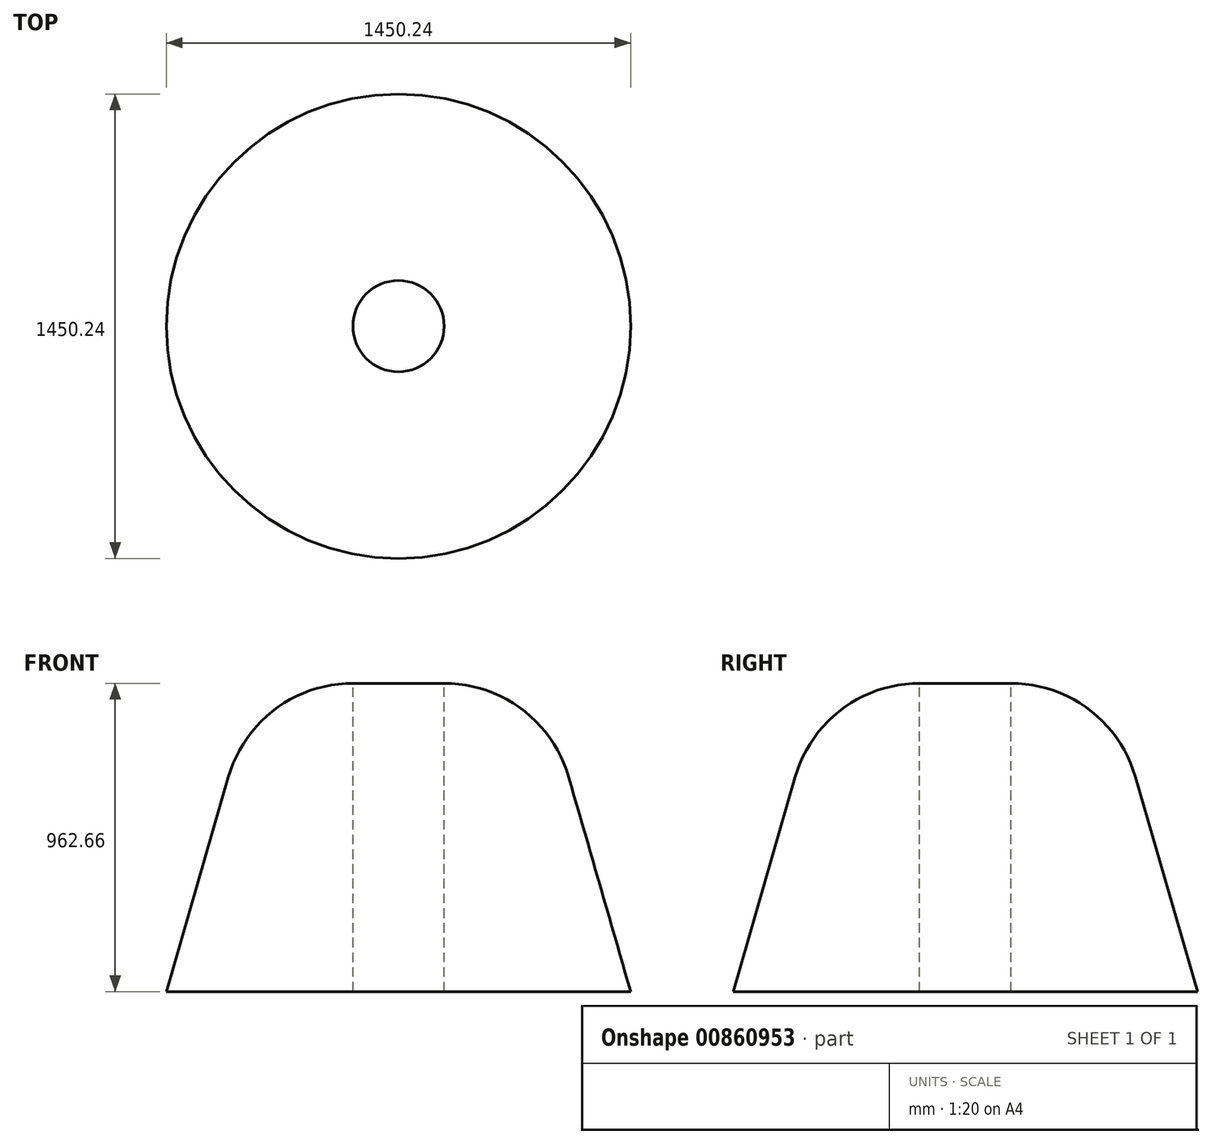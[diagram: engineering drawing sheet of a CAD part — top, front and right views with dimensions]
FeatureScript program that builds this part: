
annotation { "Feature Type Name" : "Feature", "Feature Type Description" : "" }
export const myFeature = defineFeature(function(context is Context, id is Id, definition is map)
    precondition{}
    {
        {
            var Q0;
            Q0=qCreatedBy(makeId("Top.planeOp"),FACE);
            var sketch = newSketch(context, id + "F0", { "sketchPlane" : qUnion([Q0])});
            skCircle(sketch, "E0", {"center": v(0, 0) * mm, "radius": 725.12 * mm});
            skSolve(sketch);
        }
        {
            var Q0;
            Q0=makeQuery(id+"F0.imprint","IMPRINT",FACE,{"disambiguationData":[TD([[makeQuery(id+"F0.imprint","IMPRINT",EDGE,{"derivedFrom":sQuery(id+"F0.wireOp",EDGE,"E0")}),1.0]])]});
            extrude(context, id + "F1", {"entities" : qUnion([Q0]), "depth" : 962.66 * mm, "offsetDistance" : 25.4 * mm});
        }
        {
            var Q0;
            Q0=makeQuery(id+"F1.opExtrude","CAP_FACE",FACE,{"disambiguationData":[OSD([sQuery(id+"F0.wireOp",EDGE,"E0")])],"isStart":false});
            var sketch = newSketch(context, id + "F2", { "sketchPlane" : qUnion([Q0])});
            skCircle(sketch, "E1", {"center": v(0, 0) * mm, "radius": 446.73 * mm});
            skSolve(sketch);
        }
        {
            var Q1;
            Q1=makeQuery(id+"F2.imprint","IMPRINT",FACE,{"disambiguationData":[TD([[makeQuery(id+"F2.imprint","IMPRINT",EDGE,{"derivedFrom":sQuery(id+"F2.wireOp",EDGE,"E1")}),1.0]])]});
            var Q2;
            Q2=makeQuery(id+"F1.opExtrude","CAP_FACE",FACE,{"disambiguationData":[OSD([sQuery(id+"F0.wireOp",EDGE,"E0")])],"isStart":true});
            loft(context, id + "F3", {"operationType" : NewBodyOperationType.INTERSECT, "sheetProfilesArray" : [{ "sheetProfileEntities" : qUnion([Q1]) }, { "sheetProfileEntities" : qUnion([Q2]) }]});
        }
        {
            var Q0;
            Q0=makeQuery(id+"F1.opExtrude","CAP_FACE",FACE,{"disambiguationData":[OSD([sQuery(id+"F0.wireOp",EDGE,"E0")])],"isStart":false});
            fillet(context, id + "F4", {"entities" : qUnion([Q0]), "radius" : 404.66 * mm, "tangentPropagation" : true, "allowEdgeOverflow" : false});
        }
        {
            var Q0;
            Q0=makeQuery(id+"F1.opExtrude","CAP_FACE",FACE,{"disambiguationData":[OSD([sQuery(id+"F0.wireOp",EDGE,"E0")])],"isStart":false});
            extrude(context, id + "F5", {"entities" : qUnion([Q0]), "operationType" : NewBodyOperationType.REMOVE, "oppositeDirection" : true, "depth" : 962.66 * mm, "offsetDistance" : 25.4 * mm});
        }
    });
